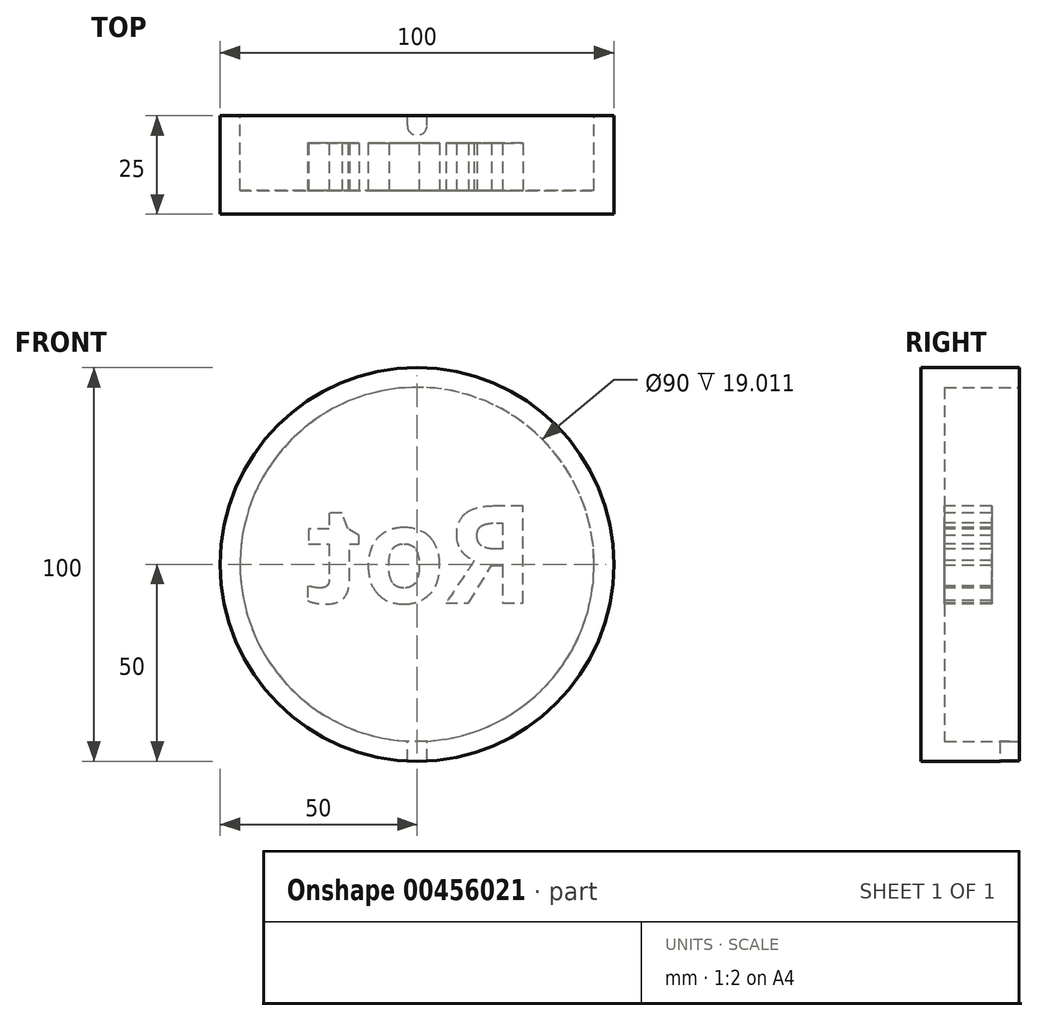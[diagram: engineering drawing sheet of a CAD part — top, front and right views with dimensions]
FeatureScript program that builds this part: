
annotation { "Feature Type Name" : "Feature", "Feature Type Description" : "" }
export const myFeature = defineFeature(function(context is Context, id is Id, definition is map)
    precondition{}
    {
        {
            var Q0;
            Q0=qCreatedBy(makeId("Top.planeOp"),FACE);
            var sketch = newSketch(context, id + "F0", { "sketchPlane" : qUnion([Q0])});
            skLineSegment(sketch, "E0", {"start": v(0, 0) * mm, "end": v(50, 0) * mm});
            skLineSegment(sketch, "E1", {"start": v(50, 0) * mm, "end": v(50, 25) * mm});
            skLineSegment(sketch, "E2", {"start": v(50, 25) * mm, "end": v(45, 25) * mm});
            skLineSegment(sketch, "E3", {"start": v(45, 25) * mm, "end": v(45, 5.99) * mm});
            skLineSegment(sketch, "E4", {"start": v(45, 5.99) * mm, "end": v(0, 5.99) * mm});
            skLineSegment(sketch, "E5", {"start": v(0, 5.99) * mm, "end": v(0, 0) * mm});
            skSolve(sketch);
        }
        {
            var Q0;
            Q0=makeQuery(id+"F0.imprint","IMPRINT",FACE,{"disambiguationData":[TD([[makeQuery(id+"F0.imprint","IMPRINT",EDGE,{"derivedFrom":sQuery(id+"F0.wireOp",EDGE,"E0")}),1.0]])]});
            var Q1;
            Q1=sQuery(id+"F0.wireOp",EDGE,"E5");
            revolve(context, id + "F1", {"entities" : qUnion([Q0]), "axis" : qUnion([Q1]), "revolveType" : RevolveType.FULL});
        }
        {
            var Q0;
            Q0=qCreatedBy(makeId("Top.planeOp"),FACE);
            var sketch = newSketch(context, id + "F2", { "sketchPlane" : qUnion([Q0])});
            skLineSegment(sketch, "E6.bottom", {"start": v(-2.47, 25) * mm, "end": v(2.53, 25) * mm});
            skLineSegment(sketch, "E6.top", {"start": v(-2.47, 20) * mm, "end": v(2.53, 20) * mm});
            skLineSegment(sketch, "E6.left", {"start": v(-2.47, 25) * mm, "end": v(-2.47, 20) * mm});
            skLineSegment(sketch, "E6.right", {"start": v(2.53, 25) * mm, "end": v(2.53, 20) * mm});
            skSolve(sketch);
        }
        {
            var Q0;
            Q0 = qSketchRegion(id + "F2", true);
            extrude(context, id + "F3", {"entities" : qUnion([Q0]), "operationType" : NewBodyOperationType.REMOVE, "endBound" : BoundingType.THROUGH_ALL, "oppositeDirection" : true, "depth" : 25.4 * mm});
        }
        {
            var Q0;
            Q0=makeQuery(id+"F3.boolean.opBoolean","COPY",EDGE,{"derivedFrom":makeQuery(id+"F3.opExtrude","SWEPT_EDGE",EDGE,{"disambiguationData":[OSD([sQuery(id+"F2.wireOp",EDGE,"E6.top"),sQuery(id+"F2.wireOp",EDGE,"E6.left")])]})});
            var Q1;
            Q1=makeQuery(id+"F3.boolean.opBoolean","COPY",EDGE,{"derivedFrom":makeQuery(id+"F3.opExtrude","SWEPT_EDGE",EDGE,{"disambiguationData":[OSD([sQuery(id+"F2.wireOp",EDGE,"E6.top"),sQuery(id+"F2.wireOp",EDGE,"E6.right")])]})});
            fillet(context, id + "F4", {"entities" : qUnion([Q0, Q1]), "radius" : 2.5 * mm, "tangentPropagation" : true, "allowEdgeOverflow" : false});
        }
        {
            var Q0;
            Q0=makeQuery(id+"F1.opRevolve","SWEPT_FACE",FACE,{"disambiguationData":[OSD([sQuery(id+"F0.wireOp",EDGE,"E4")])]});
            var sketch = newSketch(context, id + "F5", { "sketchPlane" : qUnion([Q0])});
            skText(sketch, "E7", { "text": "Rot", "fontName": "OpenSans-Bold.ttf"});
            const initialGuessF5  = {"E7": [-0.03, -0.00974, 1, 0, 0.02474]};
            skSetInitialGuess(sketch, initialGuessF5);
            skSolve(sketch);
        }
        {
            var Q0;
            Q0=makeQuery(id+"F5.imprint","IMPRINT",FACE,{"disambiguationData":[TD([[makeQuery(id+"F5.imprint","IMPRINT",EDGE,{"derivedFrom":sQuery(id+"F5.wireOp",EDGE,"E7.sketch_text.stroke-0")}),-1.0]])]});
            var Q1;
            Q1=makeQuery(id+"F5.imprint","IMPRINT",FACE,{"disambiguationData":[TD([[makeQuery(id+"F5.imprint","IMPRINT",EDGE,{"derivedFrom":sQuery(id+"F5.wireOp",EDGE,"E7.sketch_text.stroke-19")}),-1.0]])]});
            var Q2;
            Q2=makeQuery(id+"F5.imprint","IMPRINT",FACE,{"disambiguationData":[TD([[makeQuery(id+"F5.imprint","IMPRINT",EDGE,{"derivedFrom":sQuery(id+"F5.wireOp",EDGE,"E7.sketch_text.stroke-37")}),-1.0]])]});
            extrude(context, id + "F6", {"entities" : qUnion([Q0, Q1, Q2]), "operationType" : NewBodyOperationType.ADD, "depth" : 12 * mm});
        }
    });
